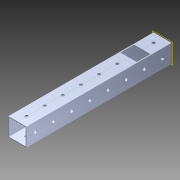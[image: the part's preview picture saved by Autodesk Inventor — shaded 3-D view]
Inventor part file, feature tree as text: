
AUTODESK INVENTOR PART (.ipt)
format: ipt  version: 2014 (Build 180170000, 170)  size: 1,203,712 bytes
history: native  units: in
note: dims shown in document units (in); Inventor stores cm internally (conversion verified against a paired STEP export)
features: extrude x2, sketch x2, pattern_circular x1, other x1, plane x1, imported_body x1
ambient origin geometry x8: Origin, YZ Plane, XZ Plane, XY Plane, X Axis, Y Axis, Z Axis, Center Point
bodies: Body1 (feature_tree)
feature tree (8):
  pattern_circular  "CirPattern2"
  other  "217-3426-STEP1"
  plane  "Work Plane1"
  extrude  "Extrusion1"  Depth=3937.0079in TaperAngle=0.0deg
  extrude  "Extrusion3"  Depth=0.75in
  imported_body  "Base1"
  sketch  "Sketch1"  dims[d0=-8.0in d1=3937.0079in d2=0.0in]
  sketch  "Sketch4"  dims[d6=0.9in d7=0.75in d8=0.3937in d9=0.0in]
